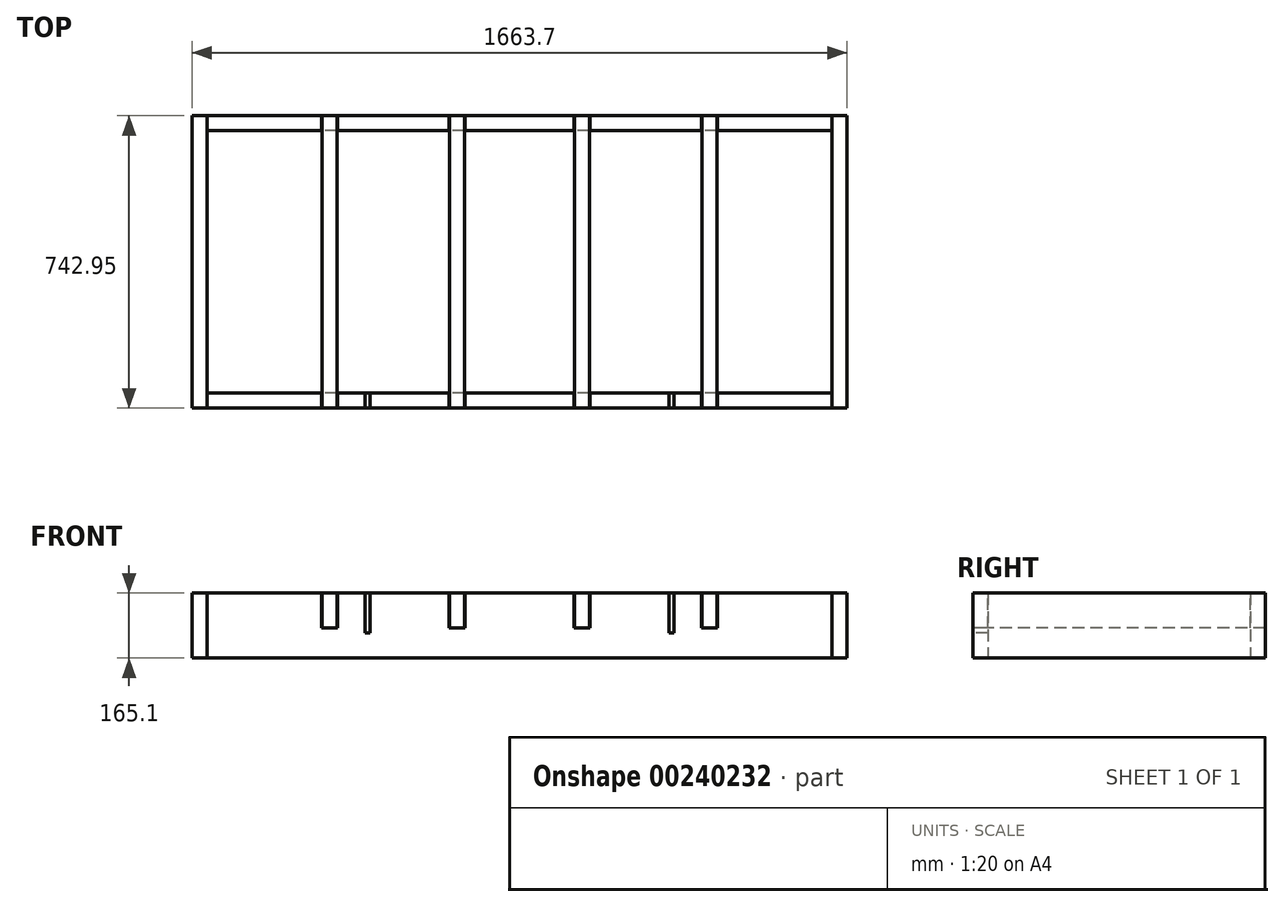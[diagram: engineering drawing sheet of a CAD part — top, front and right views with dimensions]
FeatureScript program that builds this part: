
annotation { "Feature Type Name" : "Feature", "Feature Type Description" : "" }
export const myFeature = defineFeature(function(context is Context, id is Id, definition is map)
    precondition{}
    {
        {
            var Q0;
            Q0=qCreatedBy(makeId("Top.planeOp"),FACE);
            var sketch = newSketch(context, id + "F0", { "sketchPlane" : qUnion([Q0])});
            skLineSegment(sketch, "E0.bottom", {"start": v(0, 0) * mm, "end": v(1587.5, 0) * mm});
            skLineSegment(sketch, "E0.top", {"start": v(0, -38.1) * mm, "end": v(1587.5, -38.1) * mm});
            skLineSegment(sketch, "E0.left", {"start": v(0, 0) * mm, "end": v(0, -38.1) * mm});
            skLineSegment(sketch, "E0.right", {"start": v(1587.5, 0) * mm, "end": v(1587.5, -38.1) * mm});
            skLineSegment(sketch, "E1.bottom", {"start": v(0, 704.85) * mm, "end": v(1587.5, 704.85) * mm});
            skLineSegment(sketch, "E1.top", {"start": v(0, 666.75) * mm, "end": v(1587.5, 666.75) * mm});
            skLineSegment(sketch, "E1.left", {"start": v(0, 704.85) * mm, "end": v(0, 666.75) * mm});
            skLineSegment(sketch, "E1.right", {"start": v(1587.5, 704.85) * mm, "end": v(1587.5, 666.75) * mm});
            skLineSegment(sketch, "E2.bottom", {"start": v(1587.5, 704.85) * mm, "end": v(1625.6, 704.85) * mm});
            skLineSegment(sketch, "E2.top", {"start": v(1587.5, -38.1) * mm, "end": v(1625.6, -38.1) * mm});
            skLineSegment(sketch, "E2.left", {"start": v(1587.5, 704.85) * mm, "end": v(1587.5, -38.1) * mm});
            skLineSegment(sketch, "E2.right", {"start": v(1625.6, 704.85) * mm, "end": v(1625.6, -38.1) * mm});
            skLineSegment(sketch, "E3.bottom", {"start": v(0, -38.1) * mm, "end": v(-38.1, -38.1) * mm});
            skLineSegment(sketch, "E3.top", {"start": v(0, 704.85) * mm, "end": v(-38.1, 704.85) * mm});
            skLineSegment(sketch, "E3.left", {"start": v(0, -38.1) * mm, "end": v(0, 704.85) * mm});
            skLineSegment(sketch, "E3.right", {"start": v(-38.1, -38.1) * mm, "end": v(-38.1, 704.85) * mm});
            skSolve(sketch);
        }
        {
            var Q0;
            {var subQ3=sQuery(id+"F0.wireOp",EDGE,"E3.bottom");Q0=makeQuery(id+"F0.imprint","IMPRINT",FACE,{"disambiguationData":[TD([[makeQuery(id+"F0.imprint","IMPRINT",EDGE,{"derivedFrom":subQ3}),-1.0]])]});}
            extrude(context, id + "F1", {"entities" : qUnion([Q0]), "endBound" : BoundingType.SYMMETRIC, "depth" : 165.1 * mm});
        }
        {
            var Q0;
            {var subQ0=sQuery(id+"F0.wireOp",EDGE,"E1.bottom");Q0=makeQuery(id+"F0.imprint","IMPRINT",FACE,{"disambiguationData":[TD([[makeQuery(id+"F0.imprint","IMPRINT",EDGE,{"derivedFrom":subQ0}),-1.0]])]});}
            extrude(context, id + "F2", {"entities" : qUnion([Q0]), "endBound" : BoundingType.SYMMETRIC, "depth" : 165.1 * mm});
        }
        {
            var Q0;
            {var subQ0=sQuery(id+"F0.wireOp",EDGE,"E0.bottom");Q0=makeQuery(id+"F0.imprint","IMPRINT",FACE,{"disambiguationData":[TD([[makeQuery(id+"F0.imprint","IMPRINT",EDGE,{"derivedFrom":subQ0}),-1.0]])]});}
            extrude(context, id + "F3", {"entities" : qUnion([Q0]), "endBound" : BoundingType.SYMMETRIC, "depth" : 165.1 * mm});
        }
        {
            var Q0;
            {var subQ3=sQuery(id+"F0.wireOp",EDGE,"E2.bottom");Q0=makeQuery(id+"F0.imprint","IMPRINT",FACE,{"disambiguationData":[TD([[makeQuery(id+"F0.imprint","IMPRINT",EDGE,{"derivedFrom":subQ3}),-1.0]])]});}
            extrude(context, id + "F4", {"entities" : qUnion([Q0]), "endBound" : BoundingType.SYMMETRIC, "depth" : 165.1 * mm});
        }
        {
            var Q0;
            Q0=makeQuery(id+"F3.opExtrude","SWEPT_FACE",FACE,{"disambiguationData":[OSD([sQuery(id+"F0.wireOp",EDGE,"E0.top")])]});
            var sketch = newSketch(context, id + "F5", { "sketchPlane" : qUnion([Q0])});
            skLineSegment(sketch, "E4.bottom", {"start": v(401.9, 82.55) * mm, "end": v(414.6, 82.55) * mm});
            skLineSegment(sketch, "E4.top", {"start": v(401.9, -19.05) * mm, "end": v(414.6, -19.05) * mm});
            skLineSegment(sketch, "E4.left", {"start": v(401.9, 82.55) * mm, "end": v(401.9, -19.05) * mm});
            skLineSegment(sketch, "E4.right", {"start": v(414.6, 82.55) * mm, "end": v(414.6, -19.05) * mm});
            skLineSegment(sketch, "E5.bottom", {"start": v(1173.43, 82.55) * mm, "end": v(1186.13, 82.55) * mm});
            skLineSegment(sketch, "E5.top", {"start": v(1173.43, -19.05) * mm, "end": v(1186.13, -19.05) * mm});
            skLineSegment(sketch, "E5.left", {"start": v(1173.43, 82.55) * mm, "end": v(1173.43, -19.05) * mm});
            skLineSegment(sketch, "E5.right", {"start": v(1186.13, 82.55) * mm, "end": v(1186.13, -19.05) * mm});
            skSolve(sketch);
        }
        {
            var Q0;
            Q0=makeQuery(id+"F5.imprint","IMPRINT",FACE,{"disambiguationData":[TD([[makeQuery(id+"F5.imprint","IMPRINT",EDGE,{"derivedFrom":sQuery(id+"F5.wireOp",EDGE,"E4.bottom")}),-1.0]])]});
            var Q1;
            Q1=makeQuery(id+"F5.imprint","IMPRINT",FACE,{"disambiguationData":[TD([[makeQuery(id+"F5.imprint","IMPRINT",EDGE,{"derivedFrom":sQuery(id+"F5.wireOp",EDGE,"D06HtMhc-L8Jh-q95r-K65K-Ypu8B0HC9iUq.bottom")}),-1.0]])]});
            var Q2;
            Q2=makeQuery(id+"F5.imprint","IMPRINT",FACE,{"disambiguationData":[TD([[makeQuery(id+"F5.imprint","IMPRINT",EDGE,{"derivedFrom":sQuery(id+"F5.wireOp",EDGE,"E5.bottom")}),-1.0]])]});
            var Q3;
            Q3=makeQuery(id+"F3.opExtrude","SWEPT_FACE",FACE,{"disambiguationData":[OSD([sQuery(id+"F0.wireOp",EDGE,"E0.bottom")])]});
            extrude(context, id + "F6", {"entities" : qUnion([Q0, Q1, Q2]), "operationType" : NewBodyOperationType.REMOVE, "endBound" : BoundingType.UP_TO_SURFACE, "oppositeDirection" : true, "endBoundEntityFace" : qUnion([Q3]), "depth" : 25.4 * mm});
        }
        {
            var Q0;
            Q0=makeQuery(id+"F3.opExtrude","SWEPT_FACE",FACE,{"disambiguationData":[OSD([sQuery(id+"F0.wireOp",EDGE,"E0.top")])]});
            var sketch = newSketch(context, id + "F7", { "sketchPlane" : qUnion([Q0])});
            skLineSegment(sketch, "E6", {"start": v(292.1, 82.55) * mm, "end": v(292.1, -6.35) * mm});
            skLineSegment(sketch, "E7", {"start": v(292.1, -6.35) * mm, "end": v(330.2, -6.35) * mm});
            skLineSegment(sketch, "E8", {"start": v(330.2, -6.35) * mm, "end": v(330.2, 82.55) * mm});
            skLineSegment(sketch, "E9", {"start": v(615.95, 82.55) * mm, "end": v(615.95, -6.35) * mm});
            skLineSegment(sketch, "E10", {"start": v(615.95, -6.35) * mm, "end": v(654.05, -6.35) * mm});
            skLineSegment(sketch, "E11", {"start": v(654.05, -6.35) * mm, "end": v(654.05, 82.55) * mm});
            skLineSegment(sketch, "E12", {"start": v(933.45, 82.55) * mm, "end": v(933.45, -6.35) * mm});
            skLineSegment(sketch, "E13", {"start": v(933.45, -6.35) * mm, "end": v(971.55, -6.35) * mm});
            skLineSegment(sketch, "E14", {"start": v(971.55, -6.35) * mm, "end": v(971.55, 82.55) * mm});
            skLineSegment(sketch, "E15", {"start": v(1257.3, 82.55) * mm, "end": v(1257.3, -6.35) * mm});
            skLineSegment(sketch, "E16", {"start": v(1257.3, -6.35) * mm, "end": v(1295.4, -6.35) * mm});
            skLineSegment(sketch, "E17", {"start": v(1295.4, -6.35) * mm, "end": v(1295.4, 82.55) * mm});
            skLineSegment(sketch, "E18", {"start": v(292.1, 82.55) * mm, "end": v(330.2, 82.55) * mm});
            skLineSegment(sketch, "E19", {"start": v(615.95, 82.55) * mm, "end": v(654.05, 82.55) * mm});
            skLineSegment(sketch, "E20", {"start": v(933.45, 82.55) * mm, "end": v(971.55, 82.55) * mm});
            skLineSegment(sketch, "E21", {"start": v(1257.3, 82.55) * mm, "end": v(1295.4, 82.55) * mm});
            skSolve(sketch);
        }
        {
            var Q0;
            Q0 = qSketchRegion(id + "F7", true);
            var Q1;
            Q1=makeQuery(id+"F2.opExtrude","SWEPT_FACE",FACE,{"disambiguationData":[OSD([sQuery(id+"F0.wireOp",EDGE,"E1.bottom")])]});
            extrude(context, id + "F8", {"entities" : qUnion([Q0]), "endBound" : BoundingType.UP_TO_SURFACE, "oppositeDirection" : true, "endBoundEntityFace" : qUnion([Q1]), "depth" : 749.3 * mm});
        }
        {
            var Q0;
            Q0=makeQuery(id+"F8.opExtrude","SWEPT_BODY",BODY,{"disambiguationData":[OSD([sQuery(id+"F7.wireOp",EDGE,"E6"),sQuery(id+"F7.wireOp",EDGE,"E7"),sQuery(id+"F7.wireOp",EDGE,"E8"),sQuery(id+"F7.wireOp",EDGE,"E18")])]});
            var Q1;
            Q1=makeQuery(id+"F8.opExtrude","SWEPT_BODY",BODY,{"disambiguationData":[OSD([sQuery(id+"F7.wireOp",EDGE,"E9"),sQuery(id+"F7.wireOp",EDGE,"E10"),sQuery(id+"F7.wireOp",EDGE,"E11"),sQuery(id+"F7.wireOp",EDGE,"E19")])]});
            var Q2;
            Q2=makeQuery(id+"F8.opExtrude","SWEPT_BODY",BODY,{"disambiguationData":[OSD([sQuery(id+"F7.wireOp",EDGE,"E12"),sQuery(id+"F7.wireOp",EDGE,"E13"),sQuery(id+"F7.wireOp",EDGE,"E14"),sQuery(id+"F7.wireOp",EDGE,"E20")])]});
            var Q3;
            Q3=makeQuery(id+"F8.opExtrude","SWEPT_BODY",BODY,{"disambiguationData":[OSD([sQuery(id+"F7.wireOp",EDGE,"E15"),sQuery(id+"F7.wireOp",EDGE,"E16"),sQuery(id+"F7.wireOp",EDGE,"E17"),sQuery(id+"F7.wireOp",EDGE,"E21")])]});
            var Q4;
            Q4=makeQuery(id+"F3.opExtrude","SWEPT_BODY",BODY,{"disambiguationData":[OSD([sQuery(id+"F0.wireOp",EDGE,"E0.bottom"),sQuery(id+"F0.wireOp",EDGE,"E0.top"),sQuery(id+"F0.wireOp",EDGE,"E2.left"),sQuery(id+"F0.wireOp",EDGE,"E3.left")])]});
            var Q5;
            Q5=makeQuery(id+"F2.opExtrude","SWEPT_BODY",BODY,{"disambiguationData":[OSD([sQuery(id+"F0.wireOp",EDGE,"E1.bottom"),sQuery(id+"F0.wireOp",EDGE,"E1.top"),sQuery(id+"F0.wireOp",EDGE,"E2.left"),sQuery(id+"F0.wireOp",EDGE,"E3.left")])]});
            var Q6;
            Q6=makeQuery(id+"F8.opExtrude","SWEPT_FACE",FACE,{"disambiguationData":[OSD([sQuery(id+"F7.wireOp",EDGE,"E8")])]});
            var Q7;
            Q7=makeQuery(id+"F8.opExtrude","SWEPT_FACE",FACE,{"disambiguationData":[OSD([sQuery(id+"F7.wireOp",EDGE,"E11")])]});
            var Q8;
            Q8=makeQuery(id+"F8.opExtrude","SWEPT_FACE",FACE,{"disambiguationData":[OSD([sQuery(id+"F7.wireOp",EDGE,"E14")])]});
            var Q9;
            Q9=makeQuery(id+"F8.opExtrude","SWEPT_FACE",FACE,{"disambiguationData":[OSD([sQuery(id+"F7.wireOp",EDGE,"E17")])]});
            var Q10;
            Q10=makeQuery(id+"F8.opExtrude","SWEPT_FACE",FACE,{"disambiguationData":[OSD([sQuery(id+"F7.wireOp",EDGE,"E15")])]});
            var Q11;
            Q11=makeQuery(id+"F8.opExtrude","SWEPT_FACE",FACE,{"disambiguationData":[OSD([sQuery(id+"F7.wireOp",EDGE,"E12")])]});
            var Q12;
            Q12=makeQuery(id+"F8.opExtrude","SWEPT_FACE",FACE,{"disambiguationData":[OSD([sQuery(id+"F7.wireOp",EDGE,"E9")])]});
            var Q13;
            Q13=makeQuery(id+"F8.opExtrude","SWEPT_FACE",FACE,{"disambiguationData":[OSD([sQuery(id+"F7.wireOp",EDGE,"E6")])]});
            booleanBodies(context, id + "F9", {"operationType" : BooleanOperationType.SUBTRACTION, "tools" : qUnion([Q0, Q1, Q2, Q3]), "targets" : qUnion([Q4, Q5]), "offset" : true, "entitiesToOffset" : qUnion([Q6, Q7, Q8, Q9, Q10, Q11, Q12, Q13]), "offsetDistance" : 1.59 * mm, "keepTools" : true});
        }
    });
